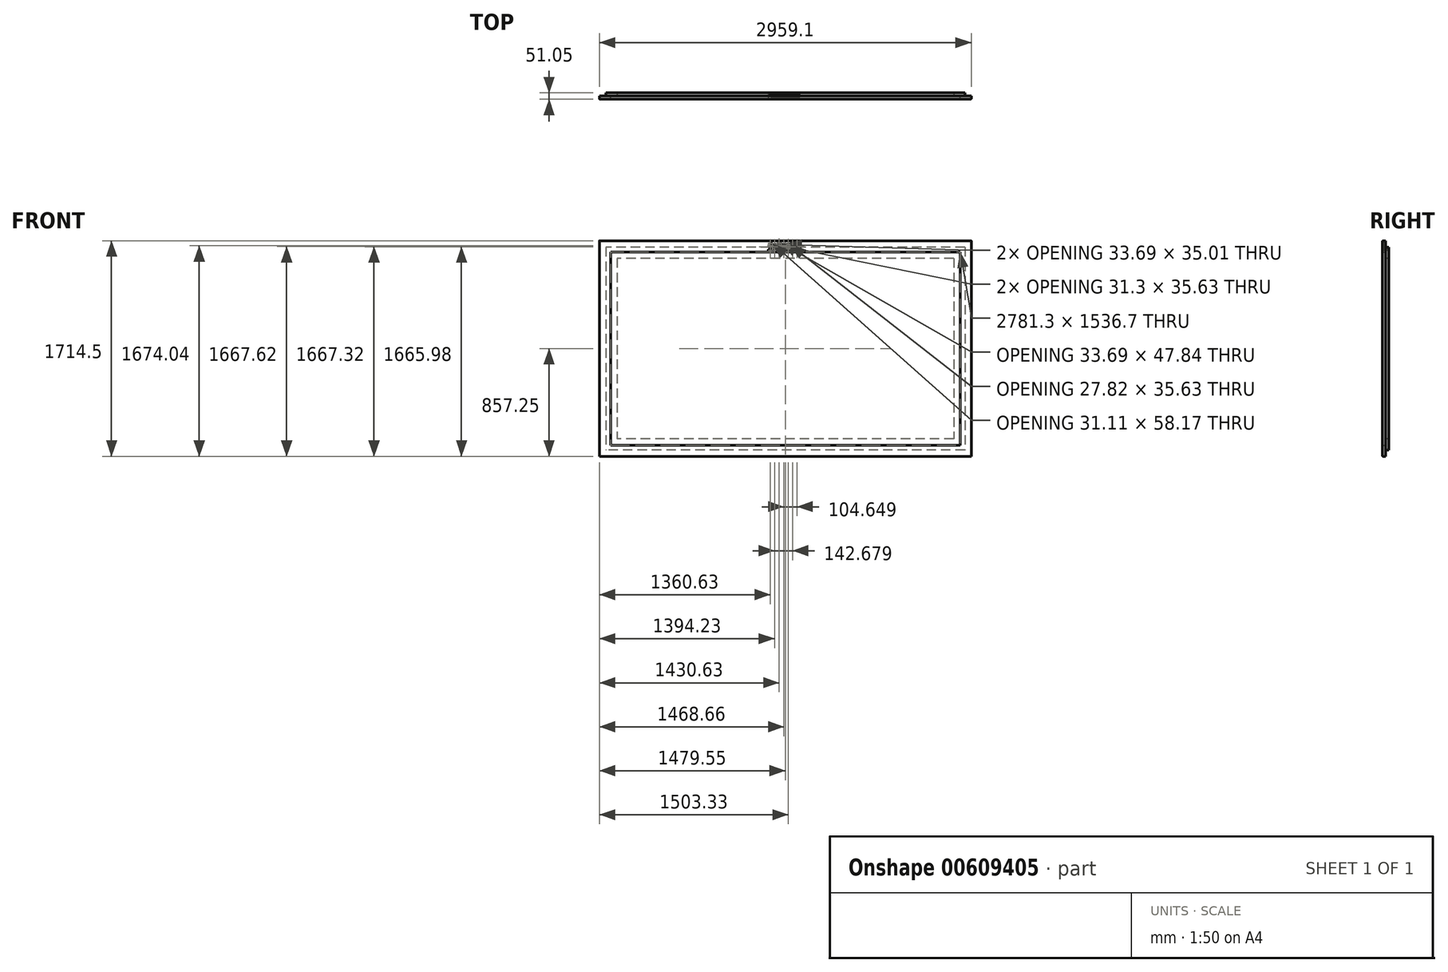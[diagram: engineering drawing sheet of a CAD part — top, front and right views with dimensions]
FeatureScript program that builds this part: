
annotation { "Feature Type Name" : "Feature", "Feature Type Description" : "" }
export const myFeature = defineFeature(function(context is Context, id is Id, definition is map)
    precondition{}
    {
        {
            var Q0;
            Q0=qCreatedBy(makeId("Front.planeOp"),FACE);
            var sketch = newSketch(context, id + "F0", { "sketchPlane" : qUnion([Q0])});
            skLineSegment(sketch, "E0.bottom", {"start": v(-1390.65, 768.35) * mm, "end": v(1390.65, 768.35) * mm});
            skLineSegment(sketch, "E0.top", {"start": v(-1390.65, -768.35) * mm, "end": v(1390.65, -768.35) * mm});
            skLineSegment(sketch, "E0.left", {"start": v(-1390.65, 768.35) * mm, "end": v(-1390.65, -768.35) * mm});
            skLineSegment(sketch, "E0.right", {"start": v(1390.65, 768.35) * mm, "end": v(1390.65, -768.35) * mm});
            skSolve(sketch);
        }
        {
            var Q0;
            Q0 = qSketchRegion(id + "F0", true);
            extrude(context, id + "F1", {"entities" : qUnion([Q0]), "depth" : 0.25 * mm, "offsetDistance" : 25.4 * mm});
        }
        {
            var Q0;
            Q0=makeQuery(id+"F1.opExtrude","CAP_FACE",FACE,{"disambiguationData":[OSD([sQuery(id+"F0.wireOp",EDGE,"E0.bottom"),sQuery(id+"F0.wireOp",EDGE,"E0.top"),sQuery(id+"F0.wireOp",EDGE,"E0.left"),sQuery(id+"F0.wireOp",EDGE,"E0.right")])],"isStart":true});
            var sketch = newSketch(context, id + "F2", { "sketchPlane" : qUnion([Q0])});
            skLineSegment(sketch, "E1.bottom", {"start": v(-1428.75, 806.45) * mm, "end": v(-1339.85, 806.45) * mm});
            skLineSegment(sketch, "E1.top", {"start": v(-1428.75, -806.45) * mm, "end": v(-1339.85, -806.45) * mm});
            skLineSegment(sketch, "E1.left", {"start": v(-1428.75, 806.45) * mm, "end": v(-1428.75, -806.45) * mm});
            skLineSegment(sketch, "E1.right", {"start": v(-1339.85, 806.45) * mm, "end": v(-1339.85, -806.45) * mm});
            skLineSegment(sketch, "E2.bottom", {"start": v(-1339.85, 806.45) * mm, "end": v(1339.85, 806.45) * mm});
            skLineSegment(sketch, "E2.top", {"start": v(-1339.85, 717.55) * mm, "end": v(1339.85, 717.55) * mm});
            skLineSegment(sketch, "E2.left", {"start": v(-1339.85, 806.45) * mm, "end": v(-1339.85, 717.55) * mm});
            skLineSegment(sketch, "E2.right", {"start": v(1339.85, 806.45) * mm, "end": v(1339.85, 717.55) * mm});
            skLineSegment(sketch, "E3.MirrorCS", {"start": v(-1339.85, -717.55) * mm, "end": v(1339.85, -717.55) * mm});
            skLineSegment(sketch, "E4.MirrorCS", {"start": v(-1339.85, -806.45) * mm, "end": v(1339.85, -806.45) * mm});
            skLineSegment(sketch, "E5.MirrorCS", {"start": v(1339.85, -806.45) * mm, "end": v(1339.85, -717.55) * mm});
            skLineSegment(sketch, "E6.MirrorCS", {"start": v(-1339.85, -806.45) * mm, "end": v(-1339.85, -717.55) * mm});
            skLineSegment(sketch, "E7.MirrorCS", {"start": v(1339.85, 806.45) * mm, "end": v(1339.85, -806.45) * mm});
            skLineSegment(sketch, "E8.MirrorCS", {"start": v(1428.75, 806.45) * mm, "end": v(1428.75, -806.45) * mm});
            skLineSegment(sketch, "E9.MirrorCS", {"start": v(1428.75, 806.45) * mm, "end": v(1339.85, 806.45) * mm});
            skLineSegment(sketch, "E10.MirrorCS", {"start": v(1428.75, -806.45) * mm, "end": v(1339.85, -806.45) * mm});
            skLineSegment(sketch, "E11.bottom", {"start": v(44.45, 717.55) * mm, "end": v(-44.45, 717.55) * mm});
            skLineSegment(sketch, "E11.top", {"start": v(44.45, -717.55) * mm, "end": v(-44.45, -717.55) * mm});
            skLineSegment(sketch, "E11.left", {"start": v(-44.45, 717.55) * mm, "end": v(-44.45, -717.55) * mm});
            skLineSegment(sketch, "E11.right", {"start": v(44.45, 717.55) * mm, "end": v(44.45, -717.55) * mm});
            skSolve(sketch);
        }
        {
            var Q0;
            {var subQ4=sQuery(id+"F2.wireOp",EDGE,"E1.bottom");Q0=makeQuery(id+"F2.imprint","IMPRINT",FACE,{"disambiguationData":[TD([[makeQuery(id+"F2.imprint","IMPRINT",EDGE,{"derivedFrom":subQ4}),-1.0]])]});}
            var Q1;
            {var subQ4=makeQuery(id+"F1.opExtrude","CAP_EDGE",EDGE,{"disambiguationData":[OSD([sQuery(id+"F0.wireOp",EDGE,"E0.right")])],"isStart":true});Q1=makeQuery(id+"F2.imprint","IMPRINT",FACE,{"disambiguationData":[TD([[makeQuery(id+"F2.imprint","IMPRINT",EDGE,{"derivedFrom":subQ4}),1.0]])]});}
            var Q2;
            {var subQ0=sQuery(id+"F2.wireOp",EDGE,"E2.top");Q2=makeQuery(id+"F2.imprint","IMPRINT",FACE,{"disambiguationData":[TD([[makeQuery(id+"F2.imprint","IMPRINT",EDGE,{"derivedFrom":subQ0}),1.0]])]});}
            var Q3;
            {var subQ0=sQuery(id+"F2.wireOp",EDGE,"E2.bottom");Q3=makeQuery(id+"F2.imprint","IMPRINT",FACE,{"disambiguationData":[TD([[makeQuery(id+"F2.imprint","IMPRINT",EDGE,{"derivedFrom":subQ0}),-1.0]])]});}
            var Q4;
            Q4=makeQuery(id+"F2.imprint","IMPRINT",FACE,{"disambiguationData":[TD([[makeQuery(id+"F2.imprint","IMPRINT",EDGE,{"derivedFrom":sQuery(id+"F2.wireOp",EDGE,"E8.MirrorCS")}),-1.0]])]});
            var Q5;
            {var subQ0=sQuery(id+"F2.wireOp",EDGE,"E4.MirrorCS");Q5=makeQuery(id+"F2.imprint","IMPRINT",FACE,{"disambiguationData":[TD([[makeQuery(id+"F2.imprint","IMPRINT",EDGE,{"derivedFrom":subQ0}),1.0]])]});}
            var Q6;
            {var subQ0=makeQuery(id+"F1.opExtrude","CAP_EDGE",EDGE,{"disambiguationData":[OSD([sQuery(id+"F0.wireOp",EDGE,"E0.left")])],"isStart":true});Q6=makeQuery(id+"F2.imprint","IMPRINT",FACE,{"disambiguationData":[TD([[makeQuery(id+"F2.imprint","IMPRINT",EDGE,{"derivedFrom":subQ0}),-1.0]])]});}
            var Q7;
            {var subQ0=sQuery(id+"F2.wireOp",EDGE,"E3.MirrorCS");Q7=makeQuery(id+"F2.imprint","IMPRINT",FACE,{"disambiguationData":[TD([[makeQuery(id+"F2.imprint","IMPRINT",EDGE,{"derivedFrom":subQ0}),-1.0]])]});}
            var Q8;
            Q8=makeQuery(id+"F2.imprint","IMPRINT",FACE,{"disambiguationData":[TD([[makeQuery(id+"F2.imprint","IMPRINT",EDGE,{"derivedFrom":sQuery(id+"F2.wireOp",EDGE,"E11.bottom")}),1.0]])]});
            extrude(context, id + "F3", {"entities" : qUnion([Q0, Q1, Q2, Q3, Q4, Q5, Q6, Q7, Q8]), "operationType" : NewBodyOperationType.ADD, "depth" : 25.4 * mm, "offsetDistance" : 25.4 * mm});
        }
        {
            var Q0;
            Q0=makeQuery(id+"F1.opExtrude","CAP_FACE",FACE,{"disambiguationData":[OSD([sQuery(id+"F0.wireOp",EDGE,"E0.bottom"),sQuery(id+"F0.wireOp",EDGE,"E0.top"),sQuery(id+"F0.wireOp",EDGE,"E0.left"),sQuery(id+"F0.wireOp",EDGE,"E0.right")])],"isStart":false});
            var sketch = newSketch(context, id + "F4", { "sketchPlane" : qUnion([Q0])});
            skPoint(sketch, "E12.0", {"position": v(-1390.65, 768.35) * mm});
            skPoint(sketch, "E13.0", {"position": v(1390.65, -768.35) * mm});
            skLineSegment(sketch, "E14.bottom", {"start": v(-1390.65, 768.35) * mm, "end": v(1390.65, 768.35) * mm});
            skLineSegment(sketch, "E14.top", {"start": v(-1390.65, -768.35) * mm, "end": v(1390.65, -768.35) * mm});
            skLineSegment(sketch, "E14.left", {"start": v(-1390.65, 768.35) * mm, "end": v(-1390.65, -768.35) * mm});
            skLineSegment(sketch, "E14.right", {"start": v(1390.65, 768.35) * mm, "end": v(1390.65, -768.35) * mm});
            skLineSegment(sketch, "E15.bottom", {"start": v(-1479.55, 857.25) * mm, "end": v(1479.55, 857.25) * mm});
            skLineSegment(sketch, "E15.top", {"start": v(-1479.55, -857.25) * mm, "end": v(1479.55, -857.25) * mm});
            skLineSegment(sketch, "E15.left", {"start": v(-1479.55, 857.25) * mm, "end": v(-1479.55, -857.25) * mm});
            skLineSegment(sketch, "E15.right", {"start": v(1479.55, 857.25) * mm, "end": v(1479.55, -857.25) * mm});
            skSolve(sketch);
        }
        {
            var Q0;
            Q0=makeQuery(id+"F4.imprint","IMPRINT",FACE,{"disambiguationData":[TD([[makeQuery(id+"F4.imprint","IMPRINT",EDGE,{"derivedFrom":sQuery(id+"F4.wireOp",EDGE,"E14.bottom")}),1.0]])]});
            extrude(context, id + "F5", {"entities" : qUnion([Q0]), "depth" : 25.4 * mm, "offsetDistance" : 25.4 * mm});
        }
        {
            var Q0;
            Q0=makeQuery(id+"F5.opExtrude","CAP_EDGE",EDGE,{"disambiguationData":[OSD([sQuery(id+"F4.wireOp",EDGE,"E15.bottom")])],"isStart":false});
            var Q1;
            Q1=makeQuery(id+"F5.opExtrude","CAP_EDGE",EDGE,{"disambiguationData":[OSD([sQuery(id+"F4.wireOp",EDGE,"E15.left")])],"isStart":false});
            var Q2;
            Q2=makeQuery(id+"F5.opExtrude","CAP_EDGE",EDGE,{"disambiguationData":[OSD([sQuery(id+"F4.wireOp",EDGE,"E15.top")])],"isStart":false});
            var Q3;
            Q3=makeQuery(id+"F5.opExtrude","CAP_EDGE",EDGE,{"disambiguationData":[OSD([sQuery(id+"F4.wireOp",EDGE,"E15.right")])],"isStart":false});
            fillet(context, id + "F6", {"entities" : qUnion([Q0, Q1, Q2, Q3]), "radius" : 6.35 * mm, "tangentPropagation" : true, "allowEdgeOverflow" : false});
        }
        {
            var Q0;
            Q0=makeQuery(id+"F5.opExtrude","CAP_FACE",FACE,{"disambiguationData":[OSD([sQuery(id+"F4.wireOp",EDGE,"E14.bottom"),sQuery(id+"F4.wireOp",EDGE,"E14.top"),sQuery(id+"F4.wireOp",EDGE,"E14.left"),sQuery(id+"F4.wireOp",EDGE,"E14.right"),sQuery(id+"F4.wireOp",EDGE,"E15.bottom"),sQuery(id+"F4.wireOp",EDGE,"E15.top"),sQuery(id+"F4.wireOp",EDGE,"E15.left"),sQuery(id+"F4.wireOp",EDGE,"E15.right")])],"isStart":false});
            var sketch = newSketch(context, id + "F7", { "sketchPlane" : qUnion([Q0])});
            skText(sketch, "E16", { "text": "Johnson", "fontName": "OpenSans-BoldItalic.ttf"});
            const initialGuessF7  = {"E16": [-0.12458, 0.79287, 1, 0, 0.04533]};
            skSetInitialGuess(sketch, initialGuessF7);
            skSolve(sketch);
        }
        {
            var Q0;
            Q0 = qSketchRegion(id + "F7", true);
            extrude(context, id + "F8", {"entities" : qUnion([Q0]), "operationType" : NewBodyOperationType.REMOVE, "endBound" : BoundingType.THROUGH_ALL, "oppositeDirection" : true, "depth" : 25.4 * mm, "offsetDistance" : 25.4 * mm});
        }
    });
